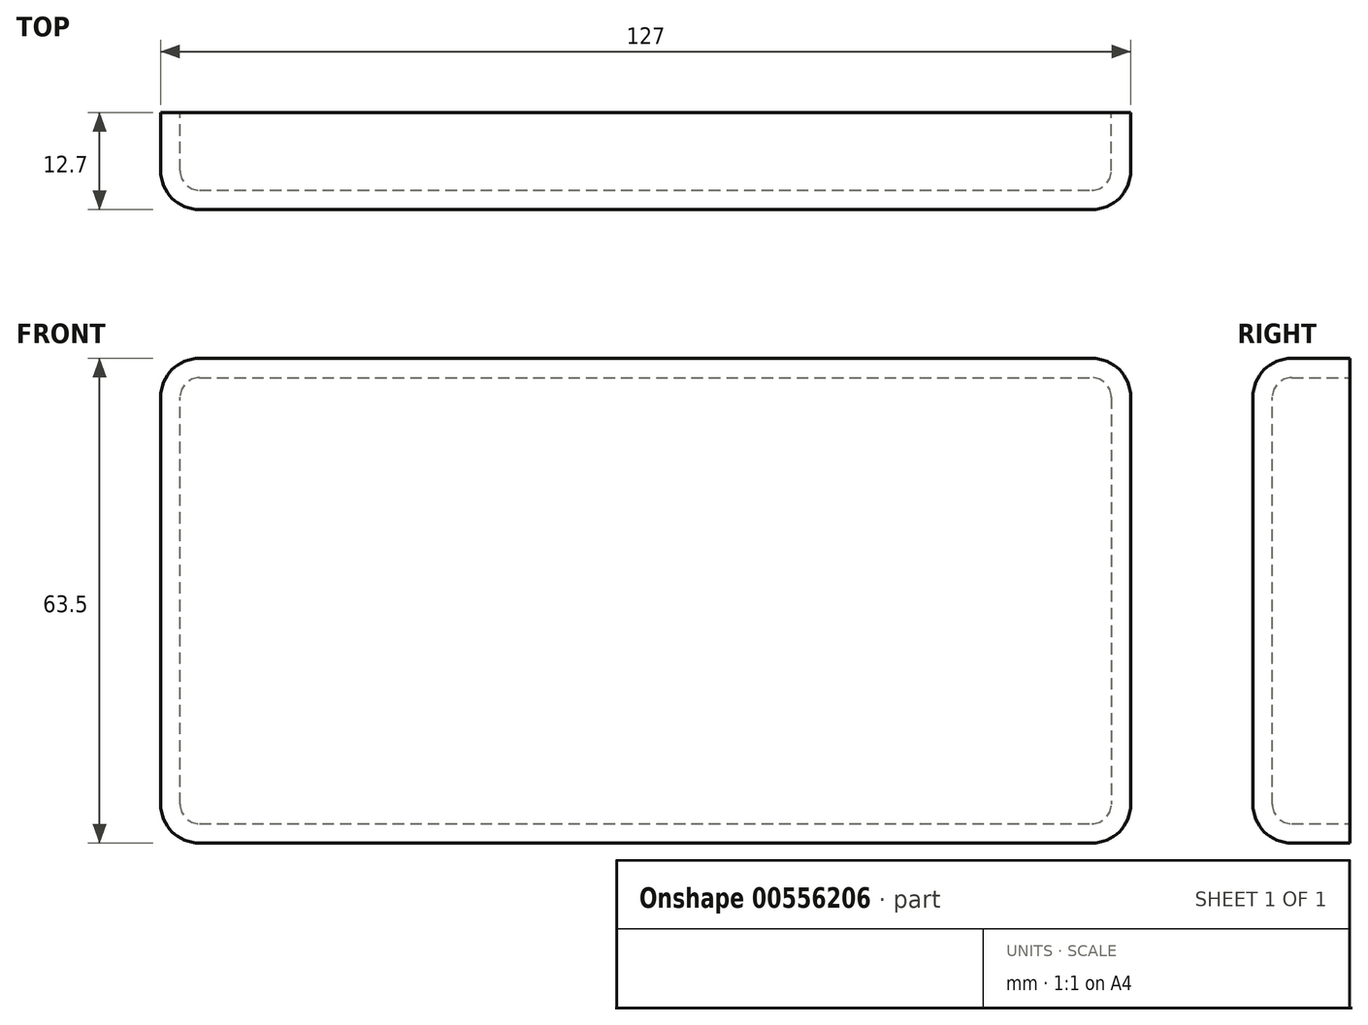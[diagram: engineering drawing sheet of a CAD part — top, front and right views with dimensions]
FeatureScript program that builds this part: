
annotation { "Feature Type Name" : "Feature", "Feature Type Description" : "" }
export const myFeature = defineFeature(function(context is Context, id is Id, definition is map)
    precondition{}
    {
        {
            var Q0;
            Q0=qCreatedBy(makeId("Front.planeOp"),FACE);
            var sketch = newSketch(context, id + "F0", { "sketchPlane" : qUnion([Q0])});
            skLineSegment(sketch, "E0", {"start": v(-63.5, -31.75) * mm, "end": v(63.5, -31.75) * mm});
            skLineSegment(sketch, "E1", {"start": v(-63.5, -31.75) * mm, "end": v(-63.5, 31.75) * mm});
            skLineSegment(sketch, "E2", {"start": v(-63.5, 31.75) * mm, "end": v(63.5, 31.75) * mm});
            skLineSegment(sketch, "E3", {"start": v(63.5, 31.75) * mm, "end": v(63.5, -31.75) * mm});
            skSolve(sketch);
        }
        {
            var Q0;
            Q0 = qSketchRegion(id + "F0", true);
            extrude(context, id + "F1", {"entities" : qUnion([Q0]), "depth" : 12.7 * mm, "offsetDistance" : 25.4 * mm});
        }
        {
            var Q0;
            Q0 = qSketchRegion(id + "F0", true);
            extrude(context, id + "F2", {"entities" : qUnion([Q0]), "operationType" : NewBodyOperationType.ADD, "depth" : 12.7 * mm, "offsetDistance" : 25.4 * mm});
        }
        {
            var Q0;
            Q0=makeQuery(id+"F1.opExtrude","CAP_FACE",FACE,{"disambiguationData":[OSD([sQuery(id+"F0.wireOp",EDGE,"E0"),sQuery(id+"F0.wireOp",EDGE,"E1"),sQuery(id+"F0.wireOp",EDGE,"E2"),sQuery(id+"F0.wireOp",EDGE,"E3")])],"isStart":false});
            var Q1;
            Q1=makeQuery(id+"F1.opExtrude","SWEPT_EDGE",EDGE,{"disambiguationData":[OSD([sQuery(id+"F0.wireOp",EDGE,"E2"),sQuery(id+"F0.wireOp",EDGE,"E3")])]});
            var Q2;
            Q2=makeQuery(id+"F1.opExtrude","SWEPT_EDGE",EDGE,{"disambiguationData":[OSD([sQuery(id+"F0.wireOp",EDGE,"E0"),sQuery(id+"F0.wireOp",EDGE,"E3")])]});
            var Q3;
            Q3=makeQuery(id+"F1.opExtrude","SWEPT_EDGE",EDGE,{"disambiguationData":[OSD([sQuery(id+"F0.wireOp",EDGE,"E0"),sQuery(id+"F0.wireOp",EDGE,"E1")])]});
            var Q4;
            Q4=makeQuery(id+"F1.opExtrude","SWEPT_EDGE",EDGE,{"disambiguationData":[OSD([sQuery(id+"F0.wireOp",EDGE,"E1"),sQuery(id+"F0.wireOp",EDGE,"E2")])]});
            fillet(context, id + "F3", {"entities" : qUnion([Q0, Q1, Q2, Q3, Q4]), "radius" : 5.08 * mm, "tangentPropagation" : true, "allowEdgeOverflow" : false});
        }
        {
            var Q0;
            Q0=makeQuery(id+"F1.opExtrude","CAP_FACE",FACE,{"disambiguationData":[OSD([sQuery(id+"F0.wireOp",EDGE,"E0"),sQuery(id+"F0.wireOp",EDGE,"E1"),sQuery(id+"F0.wireOp",EDGE,"E2"),sQuery(id+"F0.wireOp",EDGE,"E3")])],"isStart":true});
            shell(context, id + "F4", {"entities" : qUnion([Q0]), "thickness" : 2.54 * mm});
        }
    });
